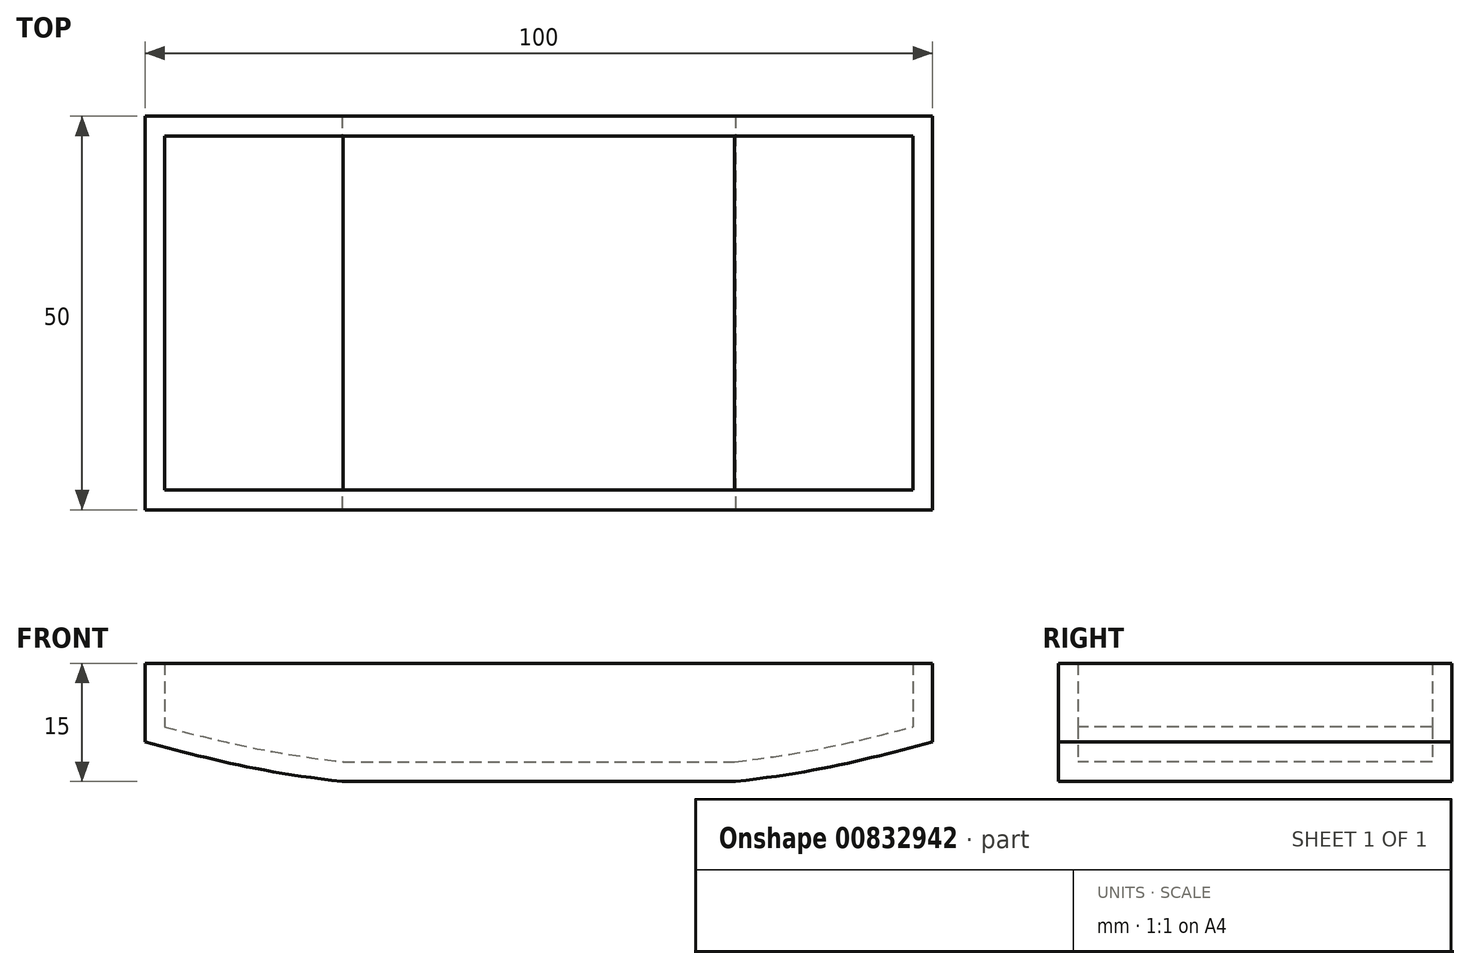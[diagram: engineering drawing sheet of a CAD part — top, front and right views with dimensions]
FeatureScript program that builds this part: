
annotation { "Feature Type Name" : "Feature", "Feature Type Description" : "" }
export const myFeature = defineFeature(function(context is Context, id is Id, definition is map)
    precondition{}
    {
        {
            var Q0;
            Q0=qCreatedBy(makeId("Front.planeOp"),FACE);
            var sketch = newSketch(context, id + "F0", { "sketchPlane" : qUnion([Q0])});
            skLineSegment(sketch, "E0", {"start": v(-50, 41.18) * mm, "end": v(50, 41.18) * mm});
            skLineSegment(sketch, "E1", {"start": v(-50, 41.18) * mm, "end": v(-50, 31.18) * mm});
            skLineSegment(sketch, "E2", {"start": v(50, 41.18) * mm, "end": v(50, 31.18) * mm});
            skLineSegment(sketch, "E3", {"start": v(-25, 26.18) * mm, "end": v(25, 26.18) * mm});
            skFitSpline(sketch, "E4", {"points": [v(-50, 31.18) * mm, v(-25, 26.18) * mm, v(25, 26.18) * mm, v(50, 31.18) * mm], "startDerivative": vector(74.3, -19.74) * mm, "endDerivative": vector(74.3, 19.74) * mm});
            skSolve(sketch);
        }
        {
            var Q0;
            Q0=makeQuery(id+"F0.imprint","IMPRINT",FACE,{"disambiguationData":[TD([[makeQuery(id+"F0.imprint","IMPRINT",EDGE,{"derivedFrom":sQuery(id+"F0.wireOp",EDGE,"E0")}),-1.0]])]});
            extrude(context, id + "F1", {"entities" : qUnion([Q0]), "oppositeDirection" : true, "depth" : 50 * mm, "offsetDistance" : 25 * mm});
        }
        {
            var Q0;
            Q0=makeQuery(id+"F1.opExtrude","SWEPT_FACE",FACE,{"disambiguationData":[OSD([sQuery(id+"F0.wireOp",EDGE,"E0")])]});
            shell(context, id + "F2", {"entities" : qUnion([Q0]), "thickness" : 2.5 * mm});
        }
    });
